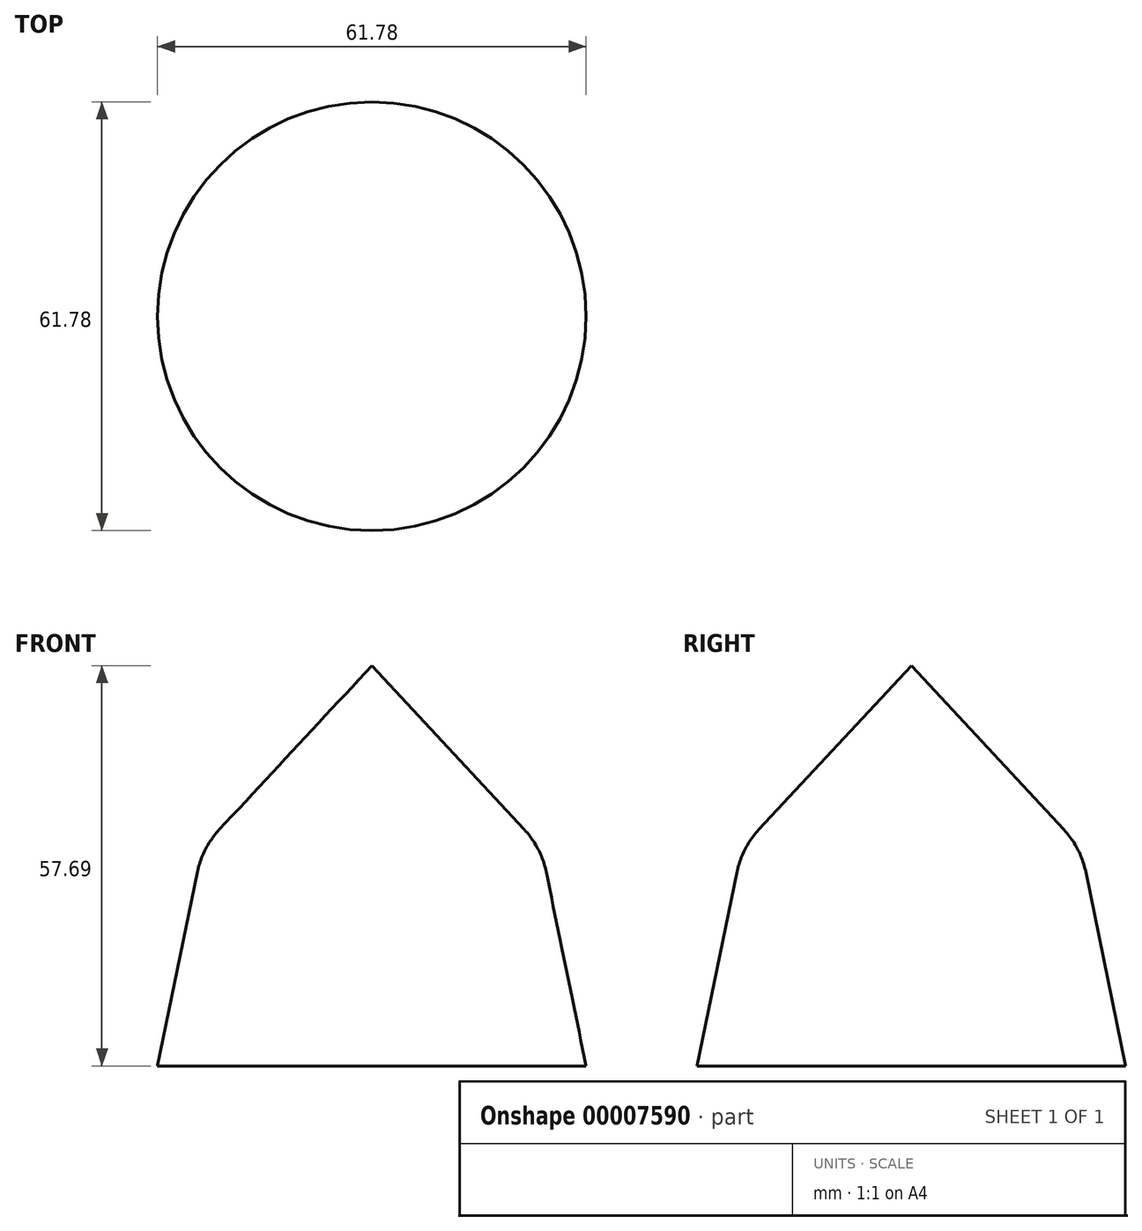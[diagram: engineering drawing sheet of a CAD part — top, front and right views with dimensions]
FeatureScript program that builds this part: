
annotation { "Feature Type Name" : "Feature", "Feature Type Description" : "" }
export const myFeature = defineFeature(function(context is Context, id is Id, definition is map)
    precondition{}
    {
        {
            var Q0;
            Q0=qCreatedBy(makeId("Front.planeOp"),FACE);
            var sketch = newSketch(context, id + "F0", { "sketchPlane" : qUnion([Q0])});
            skArc(sketch, "E0", {"start": v(-22, 34.05) * mm, "mid": v(-23.99, 31.22) * mm, "end": v(-25.14, 27.96) * mm});
            skLineSegment(sketch, "E1", {"start": v(-22, 34.05) * mm, "end": v(0, 57.7) * mm});
            skLineSegment(sketch, "E2", {"start": v(0, 57.7) * mm, "end": v(0, 0) * mm});
            skLineSegment(sketch, "E3", {"start": v(0, 0) * mm, "end": v(-30.9, 0) * mm});
            skLineSegment(sketch, "E4", {"start": v(-30.9, 0) * mm, "end": v(-25.14, 27.96) * mm});
            skSolve(sketch);
        }
        {
            var Q0;
            Q0 = qSketchRegion(id + "F0", true);
            var Q1;
            Q1=sQuery(id+"F0.wireOp",EDGE,"E2");
            revolve(context, id + "F1", {"entities" : qUnion([Q0]), "axis" : qUnion([Q1]), "revolveType" : RevolveType.FULL});
        }
    });
